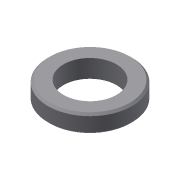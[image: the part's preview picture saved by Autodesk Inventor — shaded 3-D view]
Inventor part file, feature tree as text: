
AUTODESK INVENTOR PART (.ipt)
format: ipt  version: 2013 (Build 170138000, 138)  size: 77,312 bytes
history: native  units: in
note: dims shown in document units (in); Inventor stores cm internally (conversion verified against a paired STEP export)
features: chamfer x1, other x1, imported_body x1
ambient origin geometry x8: Origin, YZ Plane, XZ Plane, XY Plane, X Axis, Y Axis, Z Axis, Center Point
feature tree (3):
  chamfer  "Chamfer1"  [1 undecoded]
  other  "177x500 spacer_smart1"
  imported_body  "Base1"
note: 1 required parameter value undecoded (feature->parameter linkage not recoverable at this tier; creation-order binding heuristic only, values carry confidence <= 0.55)
